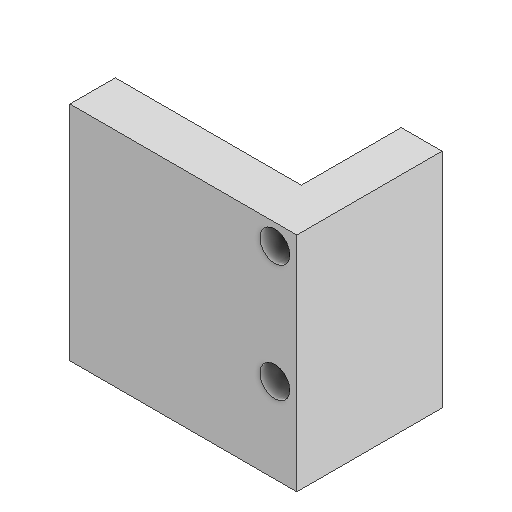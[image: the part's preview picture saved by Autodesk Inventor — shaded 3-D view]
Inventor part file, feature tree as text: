
AUTODESK INVENTOR PART (.ipt)
format: ipt  version: 2022 (Build 260153000, 153)  size: 117,760 bytes
history: native  units: mm
features: reference x11, other x6, extrude x2, sketch x2, plane x1
ambient origin geometry x8: Origin, YZ Plane, XZ Plane, XY Plane, X Axis, Y Axis, Z Axis, Center Point
bodies: Solid1 (feature_tree)
feature tree (22):
  extrude  "Extrusion1"  Depth=25.0mm
  sketch  "Sketch2"  dims[d2=3.3mm d3=5.0mm d4=0.0mm d5=5.0mm d6=0.0mm]
  plane  "Work Plane1"
  extrude  "Extrusion2"  Depth=5.0mm TaperAngle=0.0deg
  sketch  "Sketch1"  dims[d0=25.0mm d1=3.3mm]
  reference  "Reference1"
  reference  "Reference2"
  reference  "Reference3"
  reference  "Reference4"
  reference  "Reference5"
  reference  "Reference6"
  reference  "Reference7"
  reference  "Reference8"
  reference  "Reference9"
  reference  "Reference10"
  reference  "Reference11"
  other  "<userpath>\Documents\GitHub\Guinardia\INVENTOR\Assembly_Guinardia_V1.iam"
  other  "Assembly_Guinardia_V1.iam"
  other  "10_Wellplate_base_v1:1"
  other  "<userpath>\Documents\Inventor\Guinardia\INVENTOR\Assembly_Guinardia_V0.iam"
  other  "Assembly_Guinardia_V0.iam"
  other  "00_NEMA8:1"
